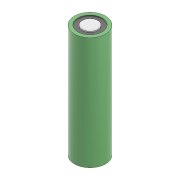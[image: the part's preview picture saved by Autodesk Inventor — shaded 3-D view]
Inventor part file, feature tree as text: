
AUTODESK INVENTOR PART (.ipt)
format: ipt  version: 2022.3 (Build 263350000, 350)  size: 110,080 bytes
history: native  units: mm
features: extrude x3, sketch x3, other x1
ambient origin geometry x8: Origin, YZ Plane, XZ Plane, XY Plane, X Axis, Y Axis, Z Axis, Center Point
bodies: Body1 (feature_tree)
feature tree (7):
  other  "Sólido1"
  extrude  "Extrusión1"  Depth=65.0mm TaperAngle=0.0deg
  extrude  "Extrusión2"  Depth=9.0mm
  extrude  "Extrusión3"  Depth=0.1mm TaperAngle=0.0deg
  sketch  "Boceto1"  dims[d0=18.0mm d1=65.0mm d2=0.0mm]
  sketch  "Boceto2"  dims[d3=9.0mm d4=14.0mm]
  sketch  "Boceto3"  dims[d5=0.5mm d6=0.0mm d7=0.1mm d8=0.0mm]
